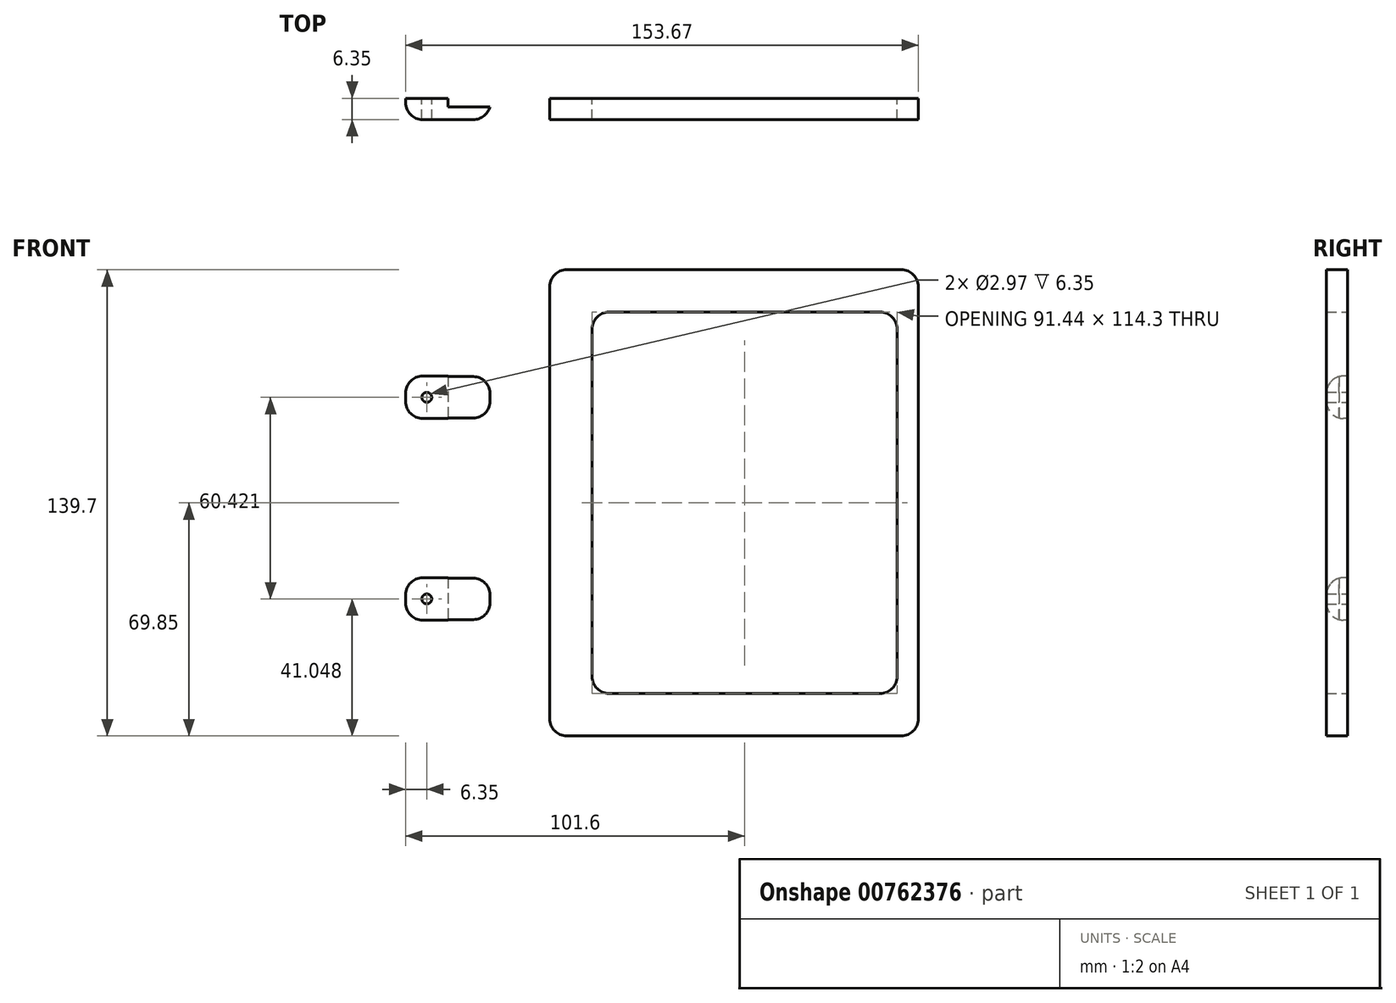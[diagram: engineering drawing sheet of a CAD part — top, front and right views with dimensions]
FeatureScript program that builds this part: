
annotation { "Feature Type Name" : "Feature", "Feature Type Description" : "" }
export const myFeature = defineFeature(function(context is Context, id is Id, definition is map)
    precondition{}
    {
        {
            var Q0;
            Q0=qCreatedBy(makeId("Front.planeOp"),FACE);
            var sketch = newSketch(context, id + "F0", { "sketchPlane" : qUnion([Q0])});
            skPoint(sketch, "E0.middle", {"position": v(0, 0) * mm});
            skLineSegment(sketch, "E1.bottom", {"start": v(45.72, 57.15) * mm, "end": v(-45.72, 57.15) * mm});
            skLineSegment(sketch, "E1.top", {"start": v(45.72, -57.15) * mm, "end": v(-45.72, -57.15) * mm});
            skLineSegment(sketch, "E1.left", {"start": v(45.72, 57.15) * mm, "end": v(45.72, -57.15) * mm});
            skLineSegment(sketch, "E2", {"start": v(-45.72, 57.15) * mm, "end": v(-45.72, -57.15) * mm});
            skLineSegment(sketch, "E3.bottom", {"start": v(52.07, 69.85) * mm, "end": v(-58.42, 69.85) * mm});
            skLineSegment(sketch, "E3.top", {"start": v(52.07, -69.85) * mm, "end": v(-58.42, -69.85) * mm});
            skLineSegment(sketch, "E3.left", {"start": v(52.07, 69.85) * mm, "end": v(52.07, -69.85) * mm});
            skLineSegment(sketch, "E3.right", {"start": v(-58.42, 69.85) * mm, "end": v(-58.42, -69.85) * mm});
            skSolve(sketch);
        }
        {
            var Q0;
            Q0=qCreatedBy(makeId("Front.planeOp"),FACE);
            var sketch = newSketch(context, id + "F1", { "sketchPlane" : qUnion([Q0])});
            skLineSegment(sketch, "E4.bottom", {"start": v(-76.2, 37.97) * mm, "end": v(-101.6, 37.97) * mm});
            skLineSegment(sketch, "E4.top", {"start": v(-76.2, 25.27) * mm, "end": v(-101.6, 25.27) * mm});
            skLineSegment(sketch, "E4.left", {"start": v(-76.2, 37.97) * mm, "end": v(-76.2, 25.27) * mm});
            skLineSegment(sketch, "E4.right", {"start": v(-101.6, 37.97) * mm, "end": v(-101.6, 25.27) * mm});
            skLineSegment(sketch, "E5.bottom", {"start": v(-76.2, -22.45) * mm, "end": v(-101.6, -22.45) * mm});
            skLineSegment(sketch, "E5.top", {"start": v(-76.2, -35.15) * mm, "end": v(-101.6, -35.15) * mm});
            skLineSegment(sketch, "E5.left", {"start": v(-76.2, -22.45) * mm, "end": v(-76.2, -35.15) * mm});
            skLineSegment(sketch, "E5.right", {"start": v(-101.6, -22.45) * mm, "end": v(-101.6, -35.15) * mm});
            skLineSegment(sketch, "E6", {"start": v(-88.9, 37.97) * mm, "end": v(-88.9, 25.27) * mm});
            skLineSegment(sketch, "E7", {"start": v(-88.9, 25.27) * mm, "end": v(-88.9, -22.45) * mm});
            skLineSegment(sketch, "E8", {"start": v(-88.9, -22.45) * mm, "end": v(-88.9, -35.15) * mm});
            skLineSegment(sketch, "E9.bottom", {"start": v(-88.95, 41.66) * mm, "end": v(-76.25, 41.66) * mm});
            skLineSegment(sketch, "E9.top", {"start": v(-88.95, 17.64) * mm, "end": v(-76.25, 17.64) * mm});
            skLineSegment(sketch, "E9.left", {"start": v(-88.95, 41.66) * mm, "end": v(-88.95, 17.64) * mm});
            skLineSegment(sketch, "E9.right", {"start": v(-76.25, 41.66) * mm, "end": v(-76.25, 17.64) * mm});
            skPoint(sketch, "E10", {"position": v(-95.25, 31.62) * mm});
            skPoint(sketch, "E11", {"position": v(-95.25, -28.8) * mm});
            skSolve(sketch);
        }
        {
            var Q0;
            Q0 = qSketchRegion(id + "F0", true);
            extrude(context, id + "F2", {"entities" : qUnion([Q0]), "depth" : 6.35 * mm, "offsetDistance" : 25.4 * mm});
        }
        {
            var Q0;
            Q0=makeQuery(id+"F2.opExtrude","SWEPT_EDGE",EDGE,{"disambiguationData":[OSD([sQuery(id+"F0.wireOp",EDGE,"E3.bottom"),sQuery(id+"F0.wireOp",EDGE,"E3.right")])]});
            var Q1;
            Q1=makeQuery(id+"F2.opExtrude","SWEPT_EDGE",EDGE,{"disambiguationData":[OSD([sQuery(id+"F0.wireOp",EDGE,"E3.top"),sQuery(id+"F0.wireOp",EDGE,"E3.right")])]});
            var Q2;
            Q2=makeQuery(id+"F2.opExtrude","SWEPT_EDGE",EDGE,{"disambiguationData":[OSD([sQuery(id+"F0.wireOp",EDGE,"E3.top"),sQuery(id+"F0.wireOp",EDGE,"E3.left")])]});
            var Q3;
            Q3=makeQuery(id+"F2.opExtrude","SWEPT_EDGE",EDGE,{"disambiguationData":[OSD([sQuery(id+"F0.wireOp",EDGE,"E3.bottom"),sQuery(id+"F0.wireOp",EDGE,"E3.left")])]});
            var Q4;
            Q4=makeQuery(id+"F2.opExtrude","SWEPT_EDGE",EDGE,{"disambiguationData":[OSD([sQuery(id+"F0.wireOp",EDGE,"E1.bottom"),sQuery(id+"F0.wireOp",EDGE,"E2")])]});
            var Q5;
            Q5=makeQuery(id+"F2.opExtrude","SWEPT_EDGE",EDGE,{"disambiguationData":[OSD([sQuery(id+"F0.wireOp",EDGE,"E1.bottom"),sQuery(id+"F0.wireOp",EDGE,"E1.left")])]});
            var Q6;
            Q6=makeQuery(id+"F2.opExtrude","SWEPT_EDGE",EDGE,{"disambiguationData":[OSD([sQuery(id+"F0.wireOp",EDGE,"E1.top"),sQuery(id+"F0.wireOp",EDGE,"E1.left")])]});
            var Q7;
            Q7=makeQuery(id+"F2.opExtrude","SWEPT_EDGE",EDGE,{"disambiguationData":[OSD([sQuery(id+"F0.wireOp",EDGE,"E1.top"),sQuery(id+"F0.wireOp",EDGE,"E2")])]});
            fillet(context, id + "F3", {"entities" : qUnion([Q0, Q1, Q2, Q3, Q4, Q5, Q6, Q7]), "radius" : 5.08 * mm, "tangentPropagation" : true, "allowEdgeOverflow" : false});
        }
        {
            var Q0;
            Q0=makeQuery(id+"F1.imprint","IMPRINT",FACE,{"disambiguationData":[TD([[makeQuery(id+"F1.imprint","IMPRINT",EDGE,{"derivedFrom":sQuery(id+"F1.wireOp",EDGE,"E4.bottom")}),1.0]])]});
            var Q1;
            Q1=makeQuery(id+"F1.imprint","IMPRINT",FACE,{"disambiguationData":[TD([[makeQuery(id+"F1.imprint","IMPRINT",EDGE,{"derivedFrom":sQuery(id+"F1.wireOp",EDGE,"E5.bottom")}),1.0]])]});
            extrude(context, id + "F4", {"entities" : qUnion([Q0, Q1]), "depth" : 6.35 * mm, "offsetDistance" : 25.4 * mm});
        }
        {
            var Q0;
            Q0=makeQuery(id+"F4.opExtrude","SWEPT_EDGE",EDGE,{"disambiguationData":[OSD([sQuery(id+"F1.wireOp",EDGE,"E4.bottom"),sQuery(id+"F1.wireOp",EDGE,"E4.right")])]});
            var Q1;
            Q1=makeQuery(id+"F4.opExtrude","CAP_EDGE",EDGE,{"disambiguationData":[OSD([sQuery(id+"F1.wireOp",EDGE,"E4.bottom")])],"isStart":false});
            var Q2;
            Q2=makeQuery(id+"F4.opExtrude","CAP_EDGE",EDGE,{"disambiguationData":[OSD([sQuery(id+"F1.wireOp",EDGE,"E4.left")])],"isStart":false});
            var Q3;
            Q3=makeQuery(id+"F4.opExtrude","CAP_EDGE",EDGE,{"disambiguationData":[OSD([sQuery(id+"F1.wireOp",EDGE,"E4.top")])],"isStart":false});
            var Q4;
            Q4=makeQuery(id+"F4.opExtrude","SWEPT_EDGE",EDGE,{"disambiguationData":[OSD([sQuery(id+"F1.wireOp",EDGE,"E4.top"),sQuery(id+"F1.wireOp",EDGE,"E4.left")])]});
            var Q5;
            Q5=makeQuery(id+"F4.opExtrude","SWEPT_EDGE",EDGE,{"disambiguationData":[OSD([sQuery(id+"F1.wireOp",EDGE,"E4.top"),sQuery(id+"F1.wireOp",EDGE,"E4.right")])]});
            var Q6;
            Q6=makeQuery(id+"F4.opExtrude","SWEPT_EDGE",EDGE,{"disambiguationData":[OSD([sQuery(id+"F1.wireOp",EDGE,"E4.bottom"),sQuery(id+"F1.wireOp",EDGE,"E4.left")])]});
            var Q7;
            Q7=makeQuery(id+"F4.opExtrude","CAP_EDGE",EDGE,{"disambiguationData":[OSD([sQuery(id+"F1.wireOp",EDGE,"E4.right")])],"isStart":false});
            fillet(context, id + "F5", {"entities" : qUnion([Q0, Q1, Q2, Q3, Q4, Q5, Q6, Q7]), "radius" : 5.08 * mm, "tangentPropagation" : true, "allowEdgeOverflow" : false});
        }
        {
            var Q0;
            Q0=makeQuery(id+"F4.opExtrude","CAP_EDGE",EDGE,{"disambiguationData":[OSD([sQuery(id+"F1.wireOp",EDGE,"E5.bottom")])],"isStart":false});
            var Q1;
            Q1=makeQuery(id+"F4.opExtrude","CAP_EDGE",EDGE,{"disambiguationData":[OSD([sQuery(id+"F1.wireOp",EDGE,"E5.left")])],"isStart":false});
            var Q2;
            Q2=makeQuery(id+"F4.opExtrude","CAP_FACE",FACE,{"disambiguationData":[OSD([sQuery(id+"F1.wireOp",EDGE,"E5.bottom"),sQuery(id+"F1.wireOp",EDGE,"E5.top"),sQuery(id+"F1.wireOp",EDGE,"E5.left"),sQuery(id+"F1.wireOp",EDGE,"E5.right")])],"isStart":false});
            var Q3;
            Q3=makeQuery(id+"F4.opExtrude","CAP_EDGE",EDGE,{"disambiguationData":[OSD([sQuery(id+"F1.wireOp",EDGE,"E5.right")])],"isStart":false});
            var Q4;
            Q4=makeQuery(id+"F4.opExtrude","SWEPT_EDGE",EDGE,{"disambiguationData":[OSD([sQuery(id+"F1.wireOp",EDGE,"E5.top"),sQuery(id+"F1.wireOp",EDGE,"E5.right")])]});
            var Q5;
            Q5=makeQuery(id+"F4.opExtrude","SWEPT_EDGE",EDGE,{"disambiguationData":[OSD([sQuery(id+"F1.wireOp",EDGE,"E5.bottom"),sQuery(id+"F1.wireOp",EDGE,"E5.right")])]});
            var Q6;
            Q6=makeQuery(id+"F4.opExtrude","SWEPT_EDGE",EDGE,{"disambiguationData":[OSD([sQuery(id+"F1.wireOp",EDGE,"E5.top"),sQuery(id+"F1.wireOp",EDGE,"E5.left")])]});
            var Q7;
            Q7=makeQuery(id+"F4.opExtrude","SWEPT_EDGE",EDGE,{"disambiguationData":[OSD([sQuery(id+"F1.wireOp",EDGE,"E5.bottom"),sQuery(id+"F1.wireOp",EDGE,"E5.left")])]});
            fillet(context, id + "F6", {"entities" : qUnion([Q0, Q1, Q2, Q3, Q4, Q5, Q6, Q7]), "radius" : 5.08 * mm, "tangentPropagation" : true, "allowEdgeOverflow" : false});
        }
        {
            var Q0;
            Q0=qCreatedBy(makeId("Front.planeOp"),FACE);
            var sketch = newSketch(context, id + "F7", { "sketchPlane" : qUnion([Q0])});
            skLineSegment(sketch, "E12.bottom", {"start": v(-88.9, 39.16) * mm, "end": v(-76.2, 39.16) * mm});
            skLineSegment(sketch, "E12.top", {"start": v(-88.9, 23.92) * mm, "end": v(-76.2, 23.92) * mm});
            skLineSegment(sketch, "E12.left", {"start": v(-88.9, 39.16) * mm, "end": v(-88.9, 23.92) * mm});
            skLineSegment(sketch, "E12.right", {"start": v(-76.2, 39.16) * mm, "end": v(-76.2, 23.92) * mm});
            skLineSegment(sketch, "E13.bottom", {"start": v(-88.9, -20.9) * mm, "end": v(-76.2, -20.9) * mm});
            skLineSegment(sketch, "E13.top", {"start": v(-88.9, -36.14) * mm, "end": v(-76.2, -36.14) * mm});
            skLineSegment(sketch, "E13.left", {"start": v(-88.9, -20.9) * mm, "end": v(-88.9, -36.14) * mm});
            skLineSegment(sketch, "E13.right", {"start": v(-76.2, -20.9) * mm, "end": v(-76.2, -36.14) * mm});
            skSolve(sketch);
        }
        {
            var Q0;
            Q0=makeQuery(id+"F7.imprint","IMPRINT",FACE,{"disambiguationData":[TD([[makeQuery(id+"F7.imprint","IMPRINT",EDGE,{"derivedFrom":sQuery(id+"F7.wireOp",EDGE,"E12.bottom")}),-1.0]])]});
            extrude(context, id + "F8", {"entities" : qUnion([Q0]), "operationType" : NewBodyOperationType.REMOVE, "oppositeDirection" : true, "depth" : -2.54 * mm, "offsetDistance" : 25.4 * mm});
        }
        {
            var Q0;
            Q0 = qSketchRegion(id + "F7", true);
            extrude(context, id + "F9", {"entities" : qUnion([Q0]), "operationType" : NewBodyOperationType.REMOVE, "oppositeDirection" : true, "depth" : -2.54 * mm, "offsetDistance" : 25.4 * mm});
        }
        {
            var Q0;
            Q0=sQuery(id+"F1.wireOp",VERTEX,"E11");
            var Q1;
            Q1=makeQuery(id+"F4.opExtrude","SWEPT_BODY",BODY,{"disambiguationData":[OSD([sQuery(id+"F1.wireOp",EDGE,"E5.bottom"),sQuery(id+"F1.wireOp",EDGE,"E5.top"),sQuery(id+"F1.wireOp",EDGE,"E5.left"),sQuery(id+"F1.wireOp",EDGE,"E5.right")])]});
            hole(context, id + "F10", {"style" : HoleStyle.SIMPLE, "endStyle" : HoleEndStyle.THROUGH, "holeDiameter" : 2.97 * mm, "majorDiameter" : 6.35 * mm, "isTappedThrough" : true, "tappedDepth" : 12.7 * mm, "tapClearance" : 3, "locations" : qUnion([Q0]), "scope" : qUnion([Q1])});
        }
        {
            var Q0;
            Q0=sQuery(id+"F1.wireOp",VERTEX,"E10");
            var Q1;
            Q1=makeQuery(id+"F4.opExtrude","SWEPT_BODY",BODY,{"disambiguationData":[OSD([sQuery(id+"F1.wireOp",EDGE,"E4.bottom"),sQuery(id+"F1.wireOp",EDGE,"E4.top"),sQuery(id+"F1.wireOp",EDGE,"E4.left"),sQuery(id+"F1.wireOp",EDGE,"E4.right")])]});
            hole(context, id + "F11", {"style" : HoleStyle.SIMPLE, "endStyle" : HoleEndStyle.THROUGH, "oppositeDirection" : true, "holeDiameter" : 2.97 * mm, "majorDiameter" : 6.35 * mm, "isTappedThrough" : true, "tappedDepth" : 12.7 * mm, "tapClearance" : 3, "locations" : qUnion([Q0]), "scope" : qUnion([Q1])});
        }
        {
            var Q0;
            Q0=sQuery(id+"F1.wireOp",VERTEX,"E11");
            var Q1;
            Q1=makeQuery(id+"F4.opExtrude","SWEPT_BODY",BODY,{"disambiguationData":[OSD([sQuery(id+"F1.wireOp",EDGE,"E5.bottom"),sQuery(id+"F1.wireOp",EDGE,"E5.top"),sQuery(id+"F1.wireOp",EDGE,"E5.left"),sQuery(id+"F1.wireOp",EDGE,"E5.right")])]});
            hole(context, id + "F12", {"style" : HoleStyle.SIMPLE, "endStyle" : HoleEndStyle.THROUGH, "oppositeDirection" : true, "holeDiameter" : 2.97 * mm, "majorDiameter" : 6.35 * mm, "isTappedThrough" : true, "tappedDepth" : 12.7 * mm, "tapClearance" : 3, "locations" : qUnion([Q0]), "scope" : qUnion([Q1])});
        }
    });
